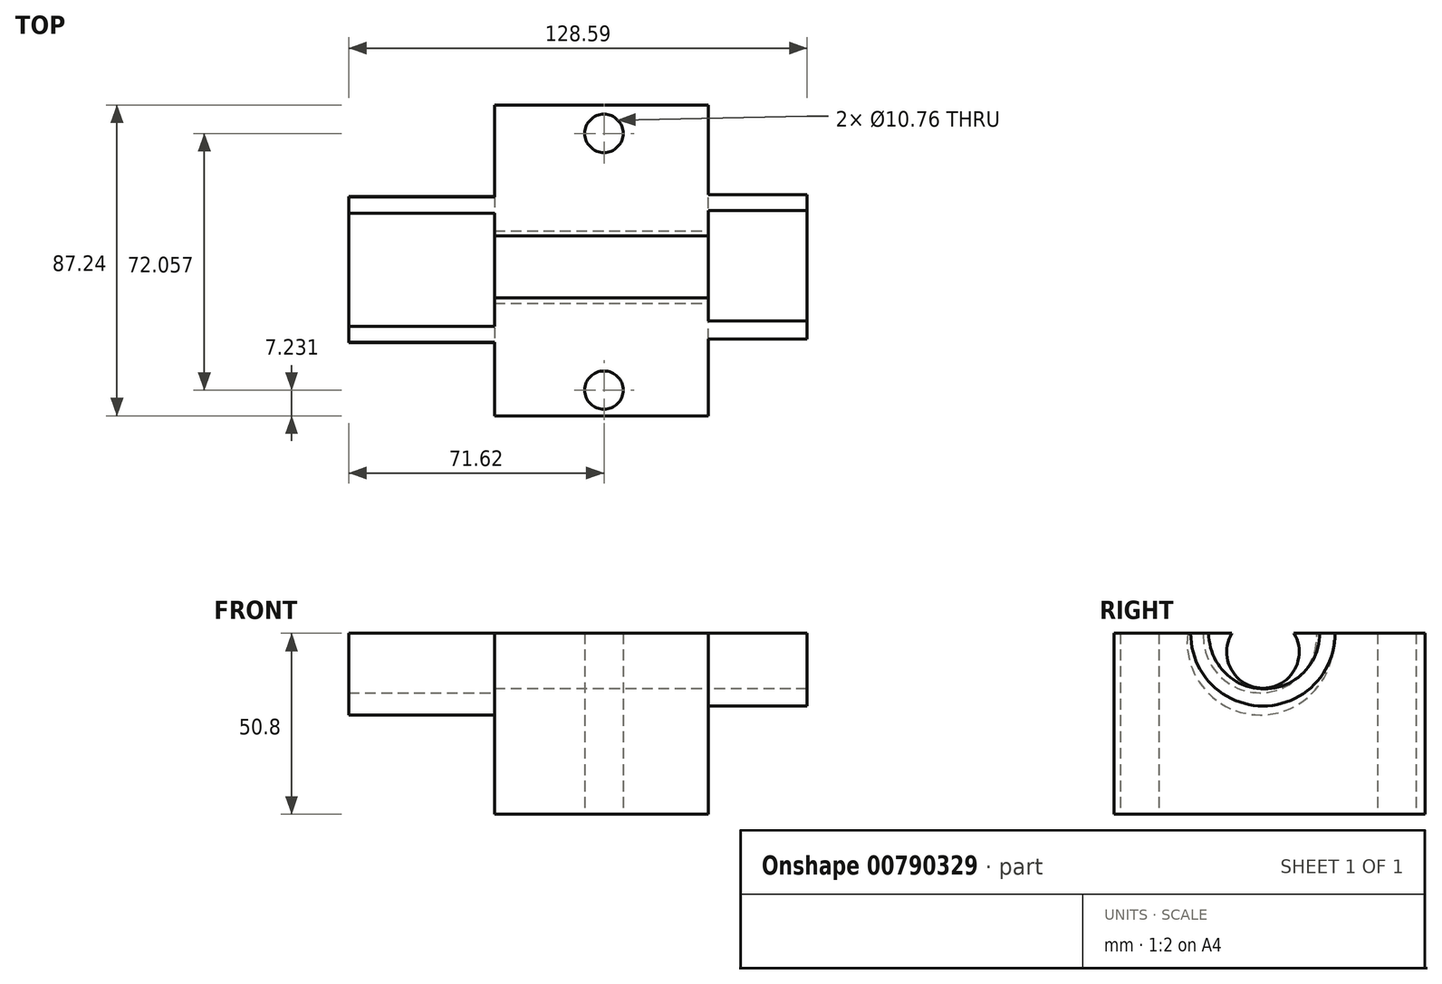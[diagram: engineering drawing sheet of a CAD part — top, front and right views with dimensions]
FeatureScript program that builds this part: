
annotation { "Feature Type Name" : "Feature", "Feature Type Description" : "" }
export const myFeature = defineFeature(function(context is Context, id is Id, definition is map)
    precondition{}
    {
        {
            var Q0;
            Q0=qCreatedBy(makeId("Top.planeOp"),FACE);
            var sketch = newSketch(context, id + "F0", { "sketchPlane" : qUnion([Q0])});
            skLineSegment(sketch, "E0", {"start": v(-30.73, 34.1) * mm, "end": v(-30.73, -53.14) * mm});
            skLineSegment(sketch, "E1", {"start": v(-30.73, -53.14) * mm, "end": v(29.28, -53.14) * mm});
            skLineSegment(sketch, "E2", {"start": v(29.28, -53.14) * mm, "end": v(29.28, 34.1) * mm});
            skLineSegment(sketch, "E3", {"start": v(29.28, 34.1) * mm, "end": v(-30.73, 34.1) * mm});
            skCircle(sketch, "E4", {"center": v(0, -45.9) * mm, "radius": 5.38 * mm});
            skCircle(sketch, "E5", {"center": v(0, 26.15) * mm, "radius": 5.38 * mm});
            skSolve(sketch);
        }
        {
            var Q0;
            Q0=makeQuery(id+"F0.imprint","IMPRINT",FACE,{"disambiguationData":[TD([[makeQuery(id+"F0.imprint","IMPRINT",EDGE,{"derivedFrom":sQuery(id+"F0.wireOp",EDGE,"E0")}),1.0]])]});
            extrude(context, id + "F1", {"entities" : qUnion([Q0]), "depth" : 50.8 * mm, "offsetDistance" : 25.4 * mm});
        }
        {
            var Q0;
            Q0=makeQuery(id+"F1.opExtrude","SWEPT_FACE",FACE,{"disambiguationData":[OSD([sQuery(id+"F0.wireOp",EDGE,"E0")])]});
            var sketch = newSketch(context, id + "F2", { "sketchPlane" : qUnion([Q0])});
            skArc(sketch, "E6", {"start": v(-3.74, 50.8) * mm, "mid": v(12.17, 34.1) * mm, "end": v(28.08, 50.8) * mm});
            skArc(sketch, "E7", {"start": v(-8.28, 50.8) * mm, "mid": v(12.1, 27.85) * mm, "end": v(32.48, 50.8) * mm});
            skSolve(sketch);
        }
        {
            var Q0;
            Q0 = qSketchRegion(id + "F2", true);
            var Q1;
            {var subQ0=sQuery(id+"F2.wireOp",EDGE,"E6");Q1=makeQuery(id+"F2.imprint","IMPRINT",FACE,{"disambiguationData":[TD([[makeQuery(id+"F2.imprint","IMPRINT",EDGE,{"derivedFrom":subQ0}),-1.0]])]});}
            extrude(context, id + "F3", {"entities" : qUnion([Q0, Q1]), "operationType" : NewBodyOperationType.ADD, "depth" : 40.9 * mm, "offsetDistance" : 25.4 * mm});
        }
        {
            var Q0;
            Q0=makeQuery(id+"F1.opExtrude","SWEPT_FACE",FACE,{"disambiguationData":[OSD([sQuery(id+"F0.wireOp",EDGE,"E2")])]});
            var sketch = newSketch(context, id + "F4", { "sketchPlane" : qUnion([Q0])});
            skArc(sketch, "E8", {"start": v(-31.6, 50.8) * mm, "mid": v(-11.36, 30.39) * mm, "end": v(8.88, 50.8) * mm});
            skArc(sketch, "E9", {"start": v(-26.55, 50.8) * mm, "mid": v(-11, 35.17) * mm, "end": v(4.54, 50.8) * mm});
            skPoint(sketch, "E10", {"position": v(-11.36, 45.53) * mm});
            skSolve(sketch);
        }
        {
            var Q0;
            Q0 = qSketchRegion(id + "F4", true);
            var Q1;
            {var subQ0=sQuery(id+"F4.wireOp",EDGE,"E8");Q1=makeQuery(id+"F4.imprint","IMPRINT",FACE,{"disambiguationData":[TD([[makeQuery(id+"F4.imprint","IMPRINT",EDGE,{"derivedFrom":subQ0}),1.0]])]});}
            extrude(context, id + "F5", {"entities" : qUnion([Q0, Q1]), "operationType" : NewBodyOperationType.ADD, "depth" : 27.7 * mm, "offsetDistance" : 25.4 * mm});
        }
        {
            var Q0;
            Q0=sQuery(id+"F4.wireOp",VERTEX,"E10");
            var Q1;
            Q1=makeQuery(id+"F1.opExtrude","SWEPT_BODY",BODY,{"disambiguationData":[OSD([sQuery(id+"F0.wireOp",EDGE,"E0"),sQuery(id+"F0.wireOp",EDGE,"E1"),sQuery(id+"F0.wireOp",EDGE,"E2"),sQuery(id+"F0.wireOp",EDGE,"E3"),sQuery(id+"F0.wireOp",EDGE,"E4"),sQuery(id+"F0.wireOp",EDGE,"E5")])]});
            hole(context, id + "F6", {"style" : HoleStyle.SIMPLE, "endStyle" : HoleEndStyle.THROUGH, "holeDiameter" : 20.32 * mm, "majorDiameter" : 6.35 * mm, "isTappedThrough" : true, "tappedDepth" : 12.7 * mm, "tapClearance" : 3, "locations" : qUnion([Q0]), "scope" : qUnion([Q1])});
        }
    });
